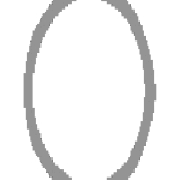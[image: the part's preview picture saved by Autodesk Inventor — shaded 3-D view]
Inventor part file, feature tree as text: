
AUTODESK INVENTOR PART (.ipt)
format: ipt  version: 2021 (Build 250183000, 183)  size: 109,568 bytes
history: native  units: in
note: dims shown in document units (in); Inventor stores cm internally (conversion verified against a paired STEP export)
features: other x4, sketch x3, plane x1
ambient origin geometry x8: Origin, YZ Plane, XZ Plane, XY Plane, X Axis, Y Axis, Z Axis, Center Point
bodies: Solid1 (feature_tree), Body (feature_tree)
feature tree (8):
  other  "Driven Length"
  other  "Frame Generator"
  other  "Start Plane"
  other  "End Plane"
  sketch  "Sketch"  dims[d2=28.9in d4=-0.0in d5=28.9in d6=0.12in d7=0.0in d10=90.0deg d9=28.9in]
  sketch  "Sketch4"  dims[d0=1.0in]
  plane  "Work Plane4"
  sketch  "Sketch5"  dims[d1=0.065in]
